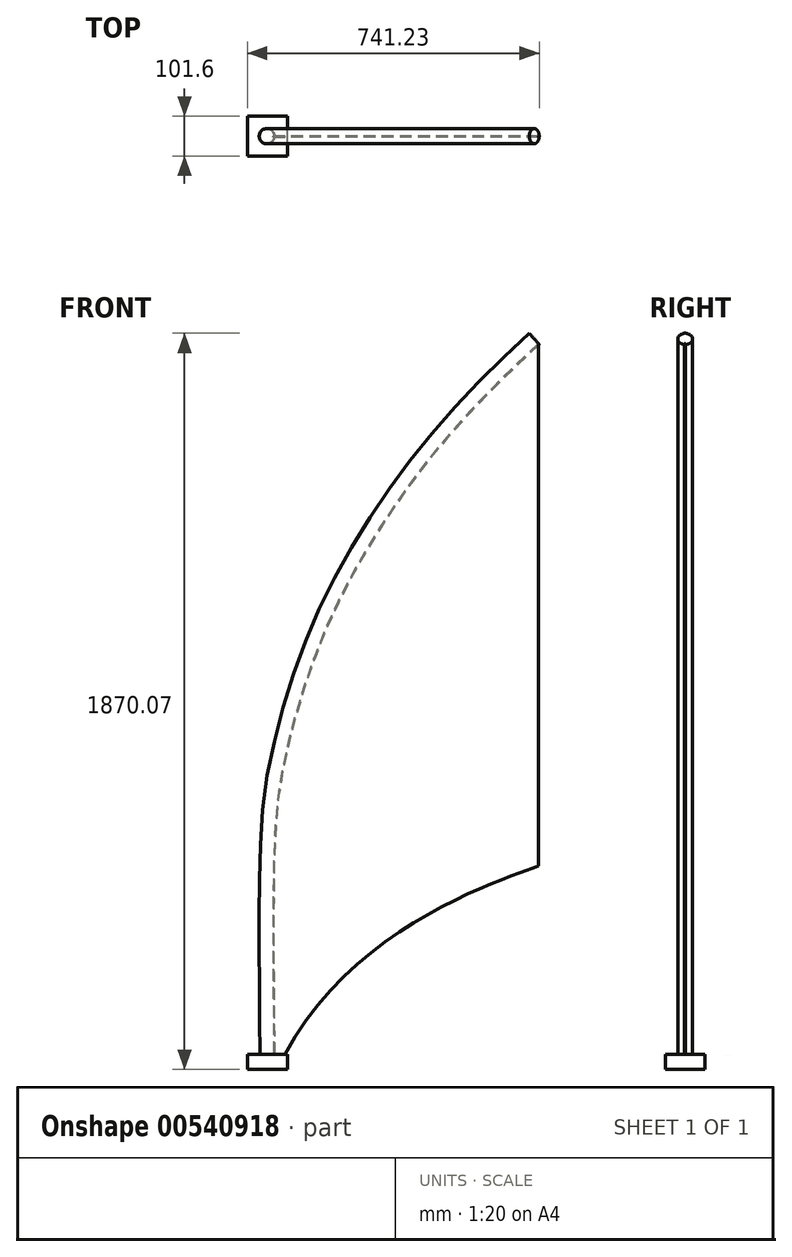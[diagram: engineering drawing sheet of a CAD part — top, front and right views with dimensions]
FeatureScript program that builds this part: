
annotation { "Feature Type Name" : "Feature", "Feature Type Description" : "" }
export const myFeature = defineFeature(function(context is Context, id is Id, definition is map)
    precondition{}
    {
        {
            var Q0;
            Q0=qCreatedBy(makeId("Front.planeOp"),FACE);
            var sketch = newSketch(context, id + "F0", { "sketchPlane" : qUnion([Q0])});
            skPoint(sketch, "E0", {"position": v(323.07, -423.6) * mm});
            skPoint(sketch, "E1", {"position": v(323.07, 903.55) * mm});
            skPoint(sketch, "E2", {"position": v(-320.8, -902.34) * mm});
            skPoint(sketch, "E3", {"position": v(-349.37, -902.34) * mm});
            skLineSegment(sketch, "E4", {"start": v(323.07, 903.55) * mm, "end": v(323.07, -423.6) * mm});
            skFitSpline(sketch, "E5", {"points": [v(323.07, -423.6) * mm, v(-320.8, -902.34) * mm], "startDerivative": vector(-90.75, -50.6) * mm, "endDerivative": vector(-555.46, -1053.48) * mm});
            skLineSegment(sketch, "E6", {"start": v(-349.37, -902.34) * mm, "end": v(-320.8, -902.34) * mm});
            skFitSpline(sketch, "E7", {"points": [v(323.07, 903.55) * mm, v(75.24, 648.45) * mm, v(-98.77, 405.58) * mm, v(-228.25, 154.18) * mm, v(-321.88, -149.86) * mm, v(-349.37, -902.34) * mm], "startDerivative": vector(-1284.05, -1165.71) * mm, "endDerivative": vector(52.06, -5401.15) * mm});
            skPoint(sketch, "E8", {"position": v(-350.03, -419.93) * mm});
            skSolve(sketch);
        }
        {
            var Q0;
            Q0 = qSketchRegion(id + "F0", true);
            extrude(context, id + "F1", {"entities" : qUnion([Q0]), "depth" : 2.54 * mm, "offsetDistance" : 25.4 * mm});
        }
        {
            var Q0;
            Q0=qCreatedBy(makeId("Right.planeOp"),FACE);
            var Q1;
            Q1=sQuery(id+"F0.wireOp",VERTEX,"E3");
            cPlane(context, id + "F2", {"entities" : qUnion([Q0, Q1]), "cplaneType" : CPlaneType.PLANE_POINT, "offset" : 25.4 * mm, "width" : 152.4 * mm, "height" : 152.4 * mm});
        }
        {
            var Q0;
            Q0=qCreatedBy(id+"F2.planeOp",FACE);
            var sketch = newSketch(context, id + "F3", { "sketchPlane" : qUnion([Q0])});
            skFitSpline(sketch, "E9.0", {"points": [v(0, 903.55) * mm, v(0, 828.95) * mm, v(0, 654) * mm, v(0, 408.83) * mm, v(0, 161.8) * mm, v(0, -227.59) * mm, v(0, -399.41) * mm, v(0, -902.33) * mm]});
            skPoint(sketch, "E10.0", {"position": v(0, -902.34) * mm});
            skSolve(sketch);
        }
        {
            var Q0;
            Q0=qCreatedBy(makeId("Top.planeOp"),FACE);
            var Q1;
            Q1=sQuery(id+"F3.wireOp",VERTEX,"E10.0");
            cPlane(context, id + "F4", {"entities" : qUnion([Q0, Q1]), "cplaneType" : CPlaneType.PLANE_POINT, "offset" : 894.08 * mm, "oppositeDirection" : true, "width" : 152.4 * mm, "height" : 152.4 * mm});
        }
        {
            var Q0;
            Q0=qCreatedBy(id+"F4.planeOp",FACE);
            var sketch = newSketch(context, id + "F5", { "sketchPlane" : qUnion([Q0])});
            skPoint(sketch, "E11.middle", {"position": v(-346.2, 0) * mm});
            skLineSegment(sketch, "E12", {"start": v(-346.2, 0) * mm, "end": v(-365.25, 0) * mm, "construction": true});
            skCircle(sketch, "E13", {"center": v(-365.25, 0) * mm, "radius": 19.05 * mm});
            skPoint(sketch, "E14.orphan", {"position": v(-377.95, -50.8) * mm});
            skPoint(sketch, "E11.top.end.orphan", {"position": v(-314.45, 50.8) * mm});
            skSolve(sketch);
        }
        {
            var Q0;
            Q0=makeQuery(id+"F5.imprint","IMPRINT",FACE,{"disambiguationData":[TD([[makeQuery(id+"F5.imprint","IMPRINT",EDGE,{"derivedFrom":sQuery(id+"F5.wireOp",EDGE,"E13")}),1.0]])]});
            var Q1;
            Q1=sQuery(id+"F0.wireOp",EDGE,"E7");
            sweep(context, id + "F6", {"profiles" : qUnion([Q0]), "path" : qUnion([Q1])});
        }
        {
            var Q0;
            Q0=makeQuery(id+"F6.opSweep","CAP_FACE",FACE,{"disambiguationData":[OSD([sQuery(id+"F0.wireOp",VERTEX,"E7.end"),sQuery(id+"F5.wireOp",EDGE,"E13")])],"isStart":true});
            var sketch = newSketch(context, id + "F7", { "sketchPlane" : qUnion([Q0])});
            skLineSegment(sketch, "E15.bottom", {"start": v(-416.05, 50.8) * mm, "end": v(-314.45, 50.8) * mm});
            skLineSegment(sketch, "E15.top", {"start": v(-416.05, -50.8) * mm, "end": v(-314.45, -50.8) * mm});
            skLineSegment(sketch, "E15.left", {"start": v(-416.05, 50.8) * mm, "end": v(-416.05, -50.8) * mm});
            skLineSegment(sketch, "E15.right", {"start": v(-314.45, 50.8) * mm, "end": v(-314.45, -50.8) * mm});
            skPoint(sketch, "E15.middle", {"position": v(-365.25, 0) * mm});
            skSolve(sketch);
        }
        {
            var Q0;
            Q0 = qSketchRegion(id + "F7", true);
            extrude(context, id + "F8", {"entities" : qUnion([Q0]), "depth" : 38.1 * mm, "offsetDistance" : 25.4 * mm});
        }
    });
